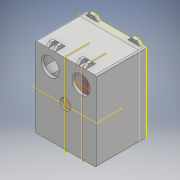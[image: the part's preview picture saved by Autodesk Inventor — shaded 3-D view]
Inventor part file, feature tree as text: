
AUTODESK INVENTOR PART (.ipt)
format: ipt  version: 2017 (Build 210142000, 142)  size: 366,080 bytes
history: native  units: mm
features: sketch x7, extrude x6, plane x4, mirror x2, fillet x1, pattern_linear x1, projected_geometry x1
ambient origin geometry x8: Origin, YZ Plane, XZ Plane, XY Plane, X Axis, Y Axis, Z Axis, Center Point
bodies: Solid1 (feature_tree)
feature tree (22):
  extrude  "Extrusion1"  Depth=100.0mm
  extrude  "Extrusion2"  Depth=4.0mm
  extrude  "Extrusion3"  Depth=4.0mm
  fillet  "Fillet1"  Radius=43.0mm
  plane  "Work Plane1"
  extrude  "Extrusion4"  Depth=43.0mm
  extrude  "Extrusion5"  Depth=23.5mm
  sketch  "Sketch9"  dims[d12=5.0mm d13=13.0mm]
  plane  "Work Plane2"
  extrude  "Extrusion6"  Depth=13.0mm
  plane  "Work Plane3"
  plane  "Work Plane5"
  pattern_linear  "Rectangular Pattern1"  Spacing1=27.0mm  [1 undecoded]
  mirror  "Mirror3"
  mirror  "Mirror4"
  sketch  "Sketch1"  dims[d0=47.0mm d1=100.0mm]
  sketch  "Sketch3"  dims[d2=3.2mm d3=4.0mm]
  sketch  "Sketch4"  dims[d4=4.0mm d5=4.0mm d6=43.0mm]
  sketch  "Sketch6"  dims[d7=3.2mm d8=43.0mm]
  sketch  "Sketch8"  dims[d9=96.0mm d11=23.5mm]
  projected_geometry  "Projected Loop1"
  sketch  "Sketch10"  dims[d14=18.0mm d15=27.0mm d16=23.0mm d17=27.0mm d18=16.0mm d19=50.0mm d20=5.0mm d21=5.0mm d22=5.0mm d23=5.0mm d24=4.0mm d25=0.0mm d30=4.0mm d31=4.0mm d32=4.0mm d33=4.0mm d34=74.0mm d35=0.0mm d36=1.0mm d37=2.0mm d38=1.0mm d39=2.0mm d40=1.0mm d41=2.0mm d42=1.0mm d43=2.0mm d44=4.0mm d45=0.0mm d46=2.0mm d47=60.0mm d48=47.0mm d49=100.0mm d50=3.2mm d51=4.0mm d52=4.0mm d53=3.2mm d55=20.0mm d57=3.2mm d58=3.2mm d61=4.0mm d62=4.0mm d63=45.0deg d64=45.0deg d65=20.0mm d66=90.0deg d67=8.0mm d68=135.0deg d69=135.0deg d70=3.2mm d71=3.2mm d72=4.0mm d73=0.0mm d74=8.0mm d77=8.0mm d80=135.0deg d81=45.0deg d82=135.0deg d83=45.0deg d84=3.2mm d85=3.2mm d86=8.0mm d89=8.0mm d91=10.0mm d92=10.0mm d93=45.0deg d94=135.0deg d95=135.0deg d96=3.2mm d97=3.2mm d98=4.0mm d99=0.0mm d100=12.0mm d101=0.0mm d102=4.0mm d103=12.0mm d104=-20.0mm d106=5.0mm d108=3.2mm d109=4.0mm d110=0.0mm d111=-45.5mm d112=-59.25mm d113=20.0mm d115=10.0mm d116=10.0mm d118=10.0mm]
note: 1 required parameter value undecoded (feature->parameter linkage not recoverable at this tier; creation-order binding heuristic only, values carry confidence <= 0.55)
